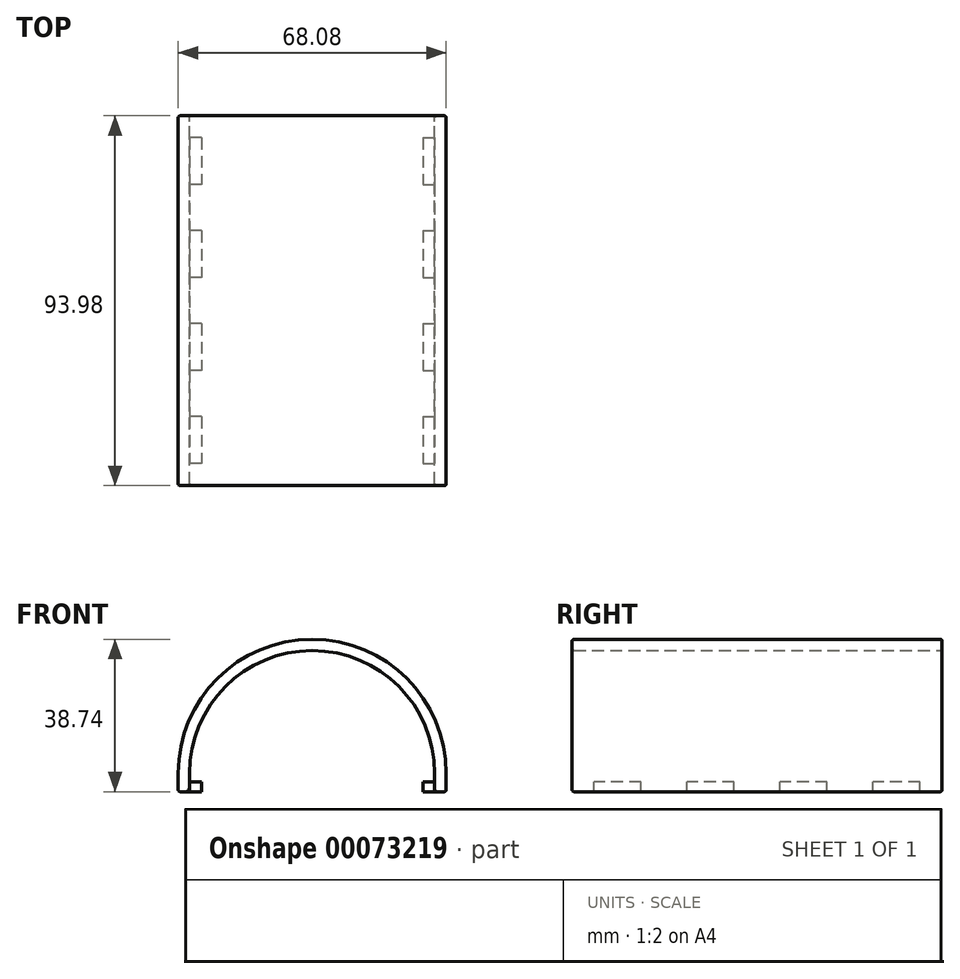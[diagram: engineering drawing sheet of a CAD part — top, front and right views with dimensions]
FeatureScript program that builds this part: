
annotation { "Feature Type Name" : "Feature", "Feature Type Description" : "" }
export const myFeature = defineFeature(function(context is Context, id is Id, definition is map)
    precondition{}
    {
        {
            var Q0;
            Q0=qCreatedBy(makeId("Front.planeOp"),FACE);
            var sketch = newSketch(context, id + "F0", { "sketchPlane" : qUnion([Q0])});
            skArc(sketch, "E0", {"start": v(31.14, 0) * mm, "mid": v(0, 31.14) * mm, "end": v(-31.14, 0) * mm});
            skArc(sketch, "E1", {"start": v(34.04, 0) * mm, "mid": v(0, 34.04) * mm, "end": v(-34.04, 0) * mm});
            skLineSegment(sketch, "E2", {"start": v(-34.04, -2.16) * mm, "end": v(-31.14, -2.16) * mm});
            skLineSegment(sketch, "E3.MirrorCS", {"start": v(34.04, -2.16) * mm, "end": v(31.14, -2.16) * mm});
            skLineSegment(sketch, "E4", {"start": v(34.04, 0) * mm, "end": v(34.04, -2.16) * mm});
            skLineSegment(sketch, "E5", {"start": v(31.14, 0) * mm, "end": v(31.14, -2.16) * mm});
            skLineSegment(sketch, "E6.MirrorCS", {"start": v(-31.14, 0) * mm, "end": v(-31.14, -2.16) * mm});
            skLineSegment(sketch, "E7.MirrorCS", {"start": v(-34.04, 0) * mm, "end": v(-34.04, -2.16) * mm});
            skSolve(sketch);
        }
        {
            var Q0;
            Q0=makeQuery(id+"F0.imprint","IMPRINT",FACE,{"disambiguationData":[TD([[makeQuery(id+"F0.imprint","IMPRINT",EDGE,{"derivedFrom":sQuery(id+"F0.wireOp",EDGE,"E0")}),-1.0]])]});
            extrude(context, id + "F1", {"entities" : qUnion([Q0]), "depth" : 93.98 * mm});
        }
        {
            var Q0;
            Q0=qCreatedBy(makeId("Top.planeOp"),FACE);
            var sketch = newSketch(context, id + "F2", { "sketchPlane" : qUnion([Q0])});
            skLineSegment(sketch, "E8.bottom", {"start": v(-31.14, -17.53) * mm, "end": v(-28.12, -17.53) * mm});
            skLineSegment(sketch, "E8.top", {"start": v(-31.14, -5.59) * mm, "end": v(-28.12, -5.59) * mm});
            skLineSegment(sketch, "E8.right", {"start": v(-28.12, -17.53) * mm, "end": v(-28.12, -5.59) * mm});
            skLineSegment(sketch, "E9.0.1.1", {"start": v(-28.12, -41.15) * mm, "end": v(-28.12, -29.21) * mm});
            skLineSegment(sketch, "E9.0.1.2", {"start": v(-31.14, -41.15) * mm, "end": v(-28.12, -41.15) * mm});
            skLineSegment(sketch, "E9.0.1.3", {"start": v(-31.14, -29.21) * mm, "end": v(-28.12, -29.21) * mm});
            skLineSegment(sketch, "E9.0.2.1", {"start": v(-28.12, -64.77) * mm, "end": v(-28.12, -52.83) * mm});
            skLineSegment(sketch, "E9.0.2.2", {"start": v(-31.14, -64.77) * mm, "end": v(-28.12, -64.77) * mm});
            skLineSegment(sketch, "E9.0.2.3", {"start": v(-31.14, -52.83) * mm, "end": v(-28.12, -52.83) * mm});
            skLineSegment(sketch, "E9.0.3.1", {"start": v(-28.12, -88.4) * mm, "end": v(-28.12, -76.45) * mm});
            skLineSegment(sketch, "E9.0.3.2", {"start": v(-31.14, -88.4) * mm, "end": v(-28.12, -88.4) * mm});
            skLineSegment(sketch, "E9.0.3.3", {"start": v(-31.14, -76.45) * mm, "end": v(-28.12, -76.45) * mm});
            skLineSegment(sketch, "E9.direction1", {"start": v(-31.14, -17.53) * mm, "end": v(-8.26, -17.53) * mm, "construction": true});
            skLineSegment(sketch, "E9.direction2", {"start": v(-31.14, -17.53) * mm, "end": v(-31.14, -41.15) * mm, "construction": true});
            skLineSegment(sketch, "E10", {"start": v(-31.14, -17.53) * mm, "end": v(-31.14, -29.21) * mm});
            skLineSegment(sketch, "E11", {"start": v(-31.14, -41.15) * mm, "end": v(-31.14, -52.83) * mm});
            skLineSegment(sketch, "E12", {"start": v(-31.14, -64.77) * mm, "end": v(-31.14, -76.45) * mm});
            skLineSegment(sketch, "E13", {"start": v(-31.14, -5.59) * mm, "end": v(-31.14, 0) * mm});
            skLineSegment(sketch, "E14", {"start": v(-31.14, 0) * mm, "end": v(-34.04, 0) * mm});
            skLineSegment(sketch, "E15", {"start": v(-34.04, 0) * mm, "end": v(-34.04, -93.98) * mm});
            skLineSegment(sketch, "E16", {"start": v(-34.04, -93.98) * mm, "end": v(-31.14, -93.98) * mm});
            skLineSegment(sketch, "E17", {"start": v(-31.14, -93.98) * mm, "end": v(-31.14, -88.4) * mm});
            skLineSegment(sketch, "E18.MirrorCS", {"start": v(31.14, -17.53) * mm, "end": v(28.12, -17.53) * mm});
            skLineSegment(sketch, "E19.MirrorCS", {"start": v(31.14, -88.4) * mm, "end": v(28.12, -88.4) * mm});
            skLineSegment(sketch, "E20.MirrorCS", {"start": v(34.04, -93.98) * mm, "end": v(31.14, -93.98) * mm});
            skLineSegment(sketch, "E21.MirrorCS", {"start": v(31.14, -41.15) * mm, "end": v(28.12, -41.15) * mm});
            skLineSegment(sketch, "E22.MirrorCS", {"start": v(31.14, -52.83) * mm, "end": v(28.12, -52.83) * mm});
            skLineSegment(sketch, "E23.MirrorCS", {"start": v(31.14, -5.59) * mm, "end": v(28.12, -5.59) * mm});
            skLineSegment(sketch, "E24.MirrorCS", {"start": v(31.14, -29.21) * mm, "end": v(28.12, -29.21) * mm});
            skLineSegment(sketch, "E25.MirrorCS", {"start": v(31.14, 0) * mm, "end": v(34.04, 0) * mm});
            skLineSegment(sketch, "E26.MirrorCS", {"start": v(31.14, -64.77) * mm, "end": v(28.12, -64.77) * mm});
            skLineSegment(sketch, "E27.MirrorCS", {"start": v(31.14, -76.45) * mm, "end": v(28.12, -76.45) * mm});
            skLineSegment(sketch, "E28.MirrorCS", {"start": v(34.04, 0) * mm, "end": v(34.04, -93.98) * mm});
            skLineSegment(sketch, "E29.MirrorCS", {"start": v(31.14, -17.53) * mm, "end": v(31.14, -41.15) * mm, "construction": true});
            skLineSegment(sketch, "E30.MirrorCS", {"start": v(28.12, -41.15) * mm, "end": v(28.12, -29.21) * mm});
            skLineSegment(sketch, "E31.MirrorCS", {"start": v(28.12, -64.77) * mm, "end": v(28.12, -52.83) * mm});
            skLineSegment(sketch, "E32.MirrorCS", {"start": v(31.14, -64.77) * mm, "end": v(31.14, -76.45) * mm});
            skLineSegment(sketch, "E33.MirrorCS", {"start": v(31.14, -5.59) * mm, "end": v(31.14, 0) * mm});
            skLineSegment(sketch, "E34.MirrorCS", {"start": v(28.12, -88.4) * mm, "end": v(28.12, -76.45) * mm});
            skLineSegment(sketch, "E35.MirrorCS", {"start": v(31.14, -17.53) * mm, "end": v(31.14, -29.21) * mm});
            skLineSegment(sketch, "E36.MirrorCS", {"start": v(31.14, -41.15) * mm, "end": v(31.14, -52.83) * mm});
            skLineSegment(sketch, "E37.MirrorCS", {"start": v(31.14, -93.98) * mm, "end": v(31.14, -88.4) * mm});
            skLineSegment(sketch, "E38.MirrorCS", {"start": v(28.12, -17.53) * mm, "end": v(28.12, -5.59) * mm});
            skSolve(sketch);
        }
        {
            var Q0;
            Q0 = qSketchRegion(id + "F2", true);
            var Q1;
            Q1=makeQuery(id+"F1.opExtrude","SWEPT_FACE",FACE,{"disambiguationData":[OSD([sQuery(id+"F0.wireOp",EDGE,"E2")])]});
            var Q2;
            Q2=makeQuery(id+"F1.opExtrude","SWEPT_FACE",FACE,{"disambiguationData":[OSD([sQuery(id+"F0.wireOp",EDGE,"E2")])]});
            extrude(context, id + "F3", {"entities" : qUnion([Q0]), "operationType" : NewBodyOperationType.ADD, "oppositeDirection" : true, "endBoundEntityFace" : qUnion([Q1]), "depth" : 4.7 * mm, "hasSecondDirection" : true, "secondDirectionBound" : SecondDirectionBoundingType.UP_TO_SURFACE, "secondDirectionOppositeDirection" : true, "secondDirectionBoundEntityFace" : qUnion([Q2]), "secondDirectionDepth" : 25.4 * mm});
        }
        {
            var Q0;
            Q0=makeQuery(id+"F3.boolean.opBoolean","MERGE",FACE,{"derivedFrom":[makeQuery(id+"F1.opExtrude","CAP_FACE",FACE,{"disambiguationData":[OSD([sQuery(id+"F0.wireOp",EDGE,"E0"),sQuery(id+"F0.wireOp",EDGE,"E1"),sQuery(id+"F0.wireOp",EDGE,"E2"),sQuery(id+"F0.wireOp",EDGE,"E3.MirrorCS"),sQuery(id+"F0.wireOp",EDGE,"E4"),sQuery(id+"F0.wireOp",EDGE,"E5"),sQuery(id+"F0.wireOp",EDGE,"E6.MirrorCS"),sQuery(id+"F0.wireOp",EDGE,"E7.MirrorCS")])],"isStart":false}),makeQuery(id+"F3.opExtrude","SWEPT_FACE",FACE,{"disambiguationData":[OSD([sQuery(id+"F2.wireOp",EDGE,"E16")])]}),makeQuery(id+"F3.opExtrude","SWEPT_FACE",FACE,{"disambiguationData":[OSD([sQuery(id+"F2.wireOp",EDGE,"E20.MirrorCS")])]})]});
            var Q1;
            Q1=makeQuery(id+"F3.boolean.opBoolean","MERGE",FACE,{"derivedFrom":[makeQuery(id+"F1.opExtrude","CAP_FACE",FACE,{"disambiguationData":[OSD([sQuery(id+"F0.wireOp",EDGE,"E0"),sQuery(id+"F0.wireOp",EDGE,"E1"),sQuery(id+"F0.wireOp",EDGE,"E2"),sQuery(id+"F0.wireOp",EDGE,"E3.MirrorCS"),sQuery(id+"F0.wireOp",EDGE,"E4"),sQuery(id+"F0.wireOp",EDGE,"E5"),sQuery(id+"F0.wireOp",EDGE,"E6.MirrorCS"),sQuery(id+"F0.wireOp",EDGE,"E7.MirrorCS")])],"isStart":true}),makeQuery(id+"F3.opExtrude","SWEPT_FACE",FACE,{"disambiguationData":[OSD([sQuery(id+"F2.wireOp",EDGE,"E14")])]}),makeQuery(id+"F3.opExtrude","SWEPT_FACE",FACE,{"disambiguationData":[OSD([sQuery(id+"F2.wireOp",EDGE,"E25.MirrorCS")])]})]});
            var Q2;
            Q2=makeQuery(id+"F3.opExtrude","CAP_EDGE",EDGE,{"disambiguationData":[OSD([sQuery(id+"F2.wireOp",EDGE,"E28.MirrorCS")])],"isStart":false});
            var Q3;
            Q3=makeQuery(id+"F3.opExtrude","CAP_EDGE",EDGE,{"disambiguationData":[OSD([sQuery(id+"F2.wireOp",EDGE,"E15")])],"isStart":false});
            fillet(context, id + "F4", {"entities" : qUnion([Q0, Q1, Q2, Q3]), "radius" : 0.5 * mm, "tangentPropagation" : true, "allowEdgeOverflow" : false});
        }
    });
